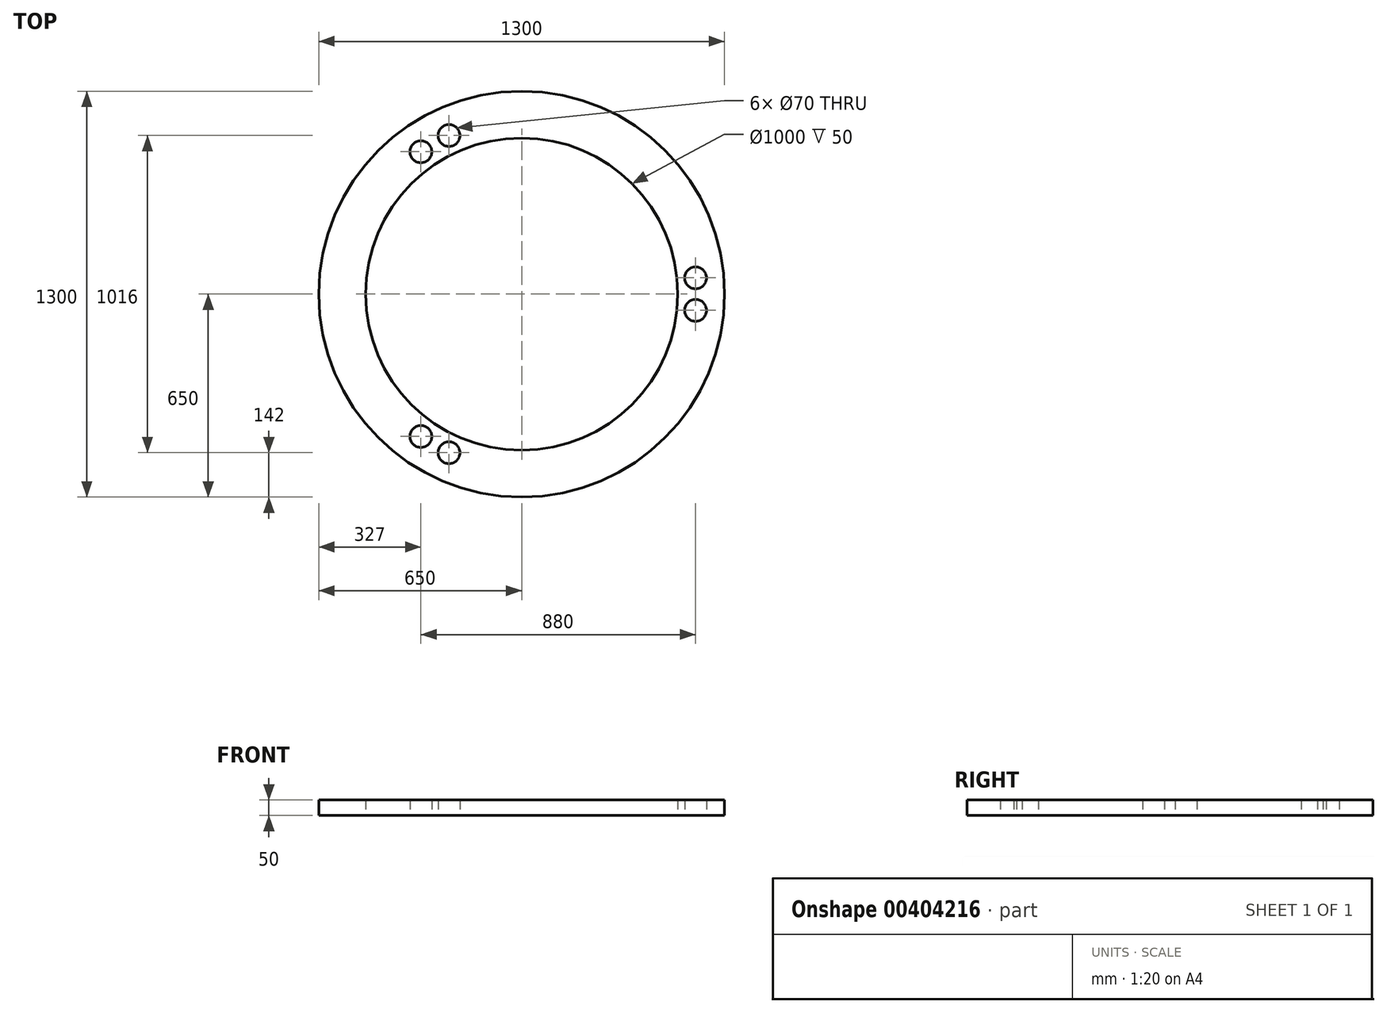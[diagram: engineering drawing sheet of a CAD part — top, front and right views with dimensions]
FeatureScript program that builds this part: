
annotation { "Feature Type Name" : "Feature", "Feature Type Description" : "" }
export const myFeature = defineFeature(function(context is Context, id is Id, definition is map)
    precondition{}
    {
        {
            var Q0;
            Q0=qCreatedBy(makeId("Top.planeOp"),FACE);
            var sketch = newSketch(context, id + "F0", { "sketchPlane" : qUnion([Q0])});
            skCircle(sketch, "E0", {"center": v(-233, -508) * mm, "radius": 35 * mm});
            skCircle(sketch, "E1", {"center": v(-233, 508) * mm, "radius": 35 * mm});
            skCircle(sketch, "E2", {"center": v(557, 52) * mm, "radius": 35 * mm});
            skCircle(sketch, "E3", {"center": v(557, -52) * mm, "radius": 35 * mm});
            skCircle(sketch, "E4", {"center": v(0, 0) * mm, "radius": 650 * mm});
            skCircle(sketch, "E5", {"center": v(-323, 456) * mm, "radius": 35 * mm});
            skCircle(sketch, "E6", {"center": v(-323, -456) * mm, "radius": 35 * mm});
            skCircle(sketch, "E7", {"center": v(0, 0) * mm, "radius": 500 * mm});
            skSolve(sketch);
        }
        {
            var Q0;
            Q0=makeQuery(id+"F0.imprint","IMPRINT",FACE,{"disambiguationData":[TD([[makeQuery(id+"F0.imprint","IMPRINT",EDGE,{"derivedFrom":sQuery(id+"F0.wireOp",EDGE,"E0")}),-1.0]])]});
            extrude(context, id + "F1", {"entities" : qUnion([Q0]), "depth" : 50 * mm});
        }
    });
